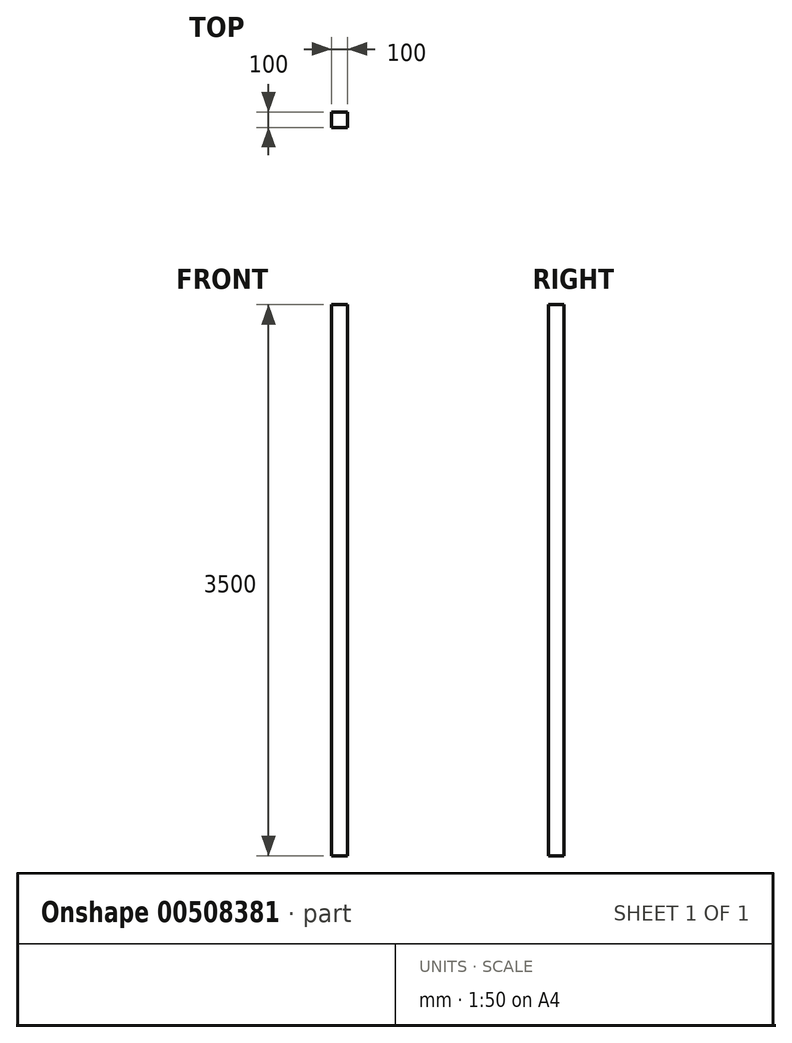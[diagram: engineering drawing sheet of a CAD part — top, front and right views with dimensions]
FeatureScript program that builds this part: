
annotation { "Feature Type Name" : "Feature", "Feature Type Description" : "" }
export const myFeature = defineFeature(function(context is Context, id is Id, definition is map)
    precondition{}
    {
        {
            var Q0;
            Q0=qCreatedBy(makeId("Top.planeOp"),FACE);
            var sketch = newSketch(context, id + "F0", { "sketchPlane" : qUnion([Q0])});
            skLineSegment(sketch, "E0.bottom", {"start": v(50, -50) * mm, "end": v(-50, -50) * mm});
            skLineSegment(sketch, "E0.top", {"start": v(50, 50) * mm, "end": v(-50, 50) * mm});
            skLineSegment(sketch, "E0.left", {"start": v(50, -50) * mm, "end": v(50, 50) * mm});
            skLineSegment(sketch, "E0.right", {"start": v(-50, -50) * mm, "end": v(-50, 50) * mm});
            skPoint(sketch, "E0.middle", {"position": v(0, 0) * mm});
            skSolve(sketch);
        }
        {
            var Q0;
            Q0 = qSketchRegion(id + "F0", true);
            extrude(context, id + "F1", {"entities" : qUnion([Q0]), "depth" : 3500 * mm});
        }
    });
